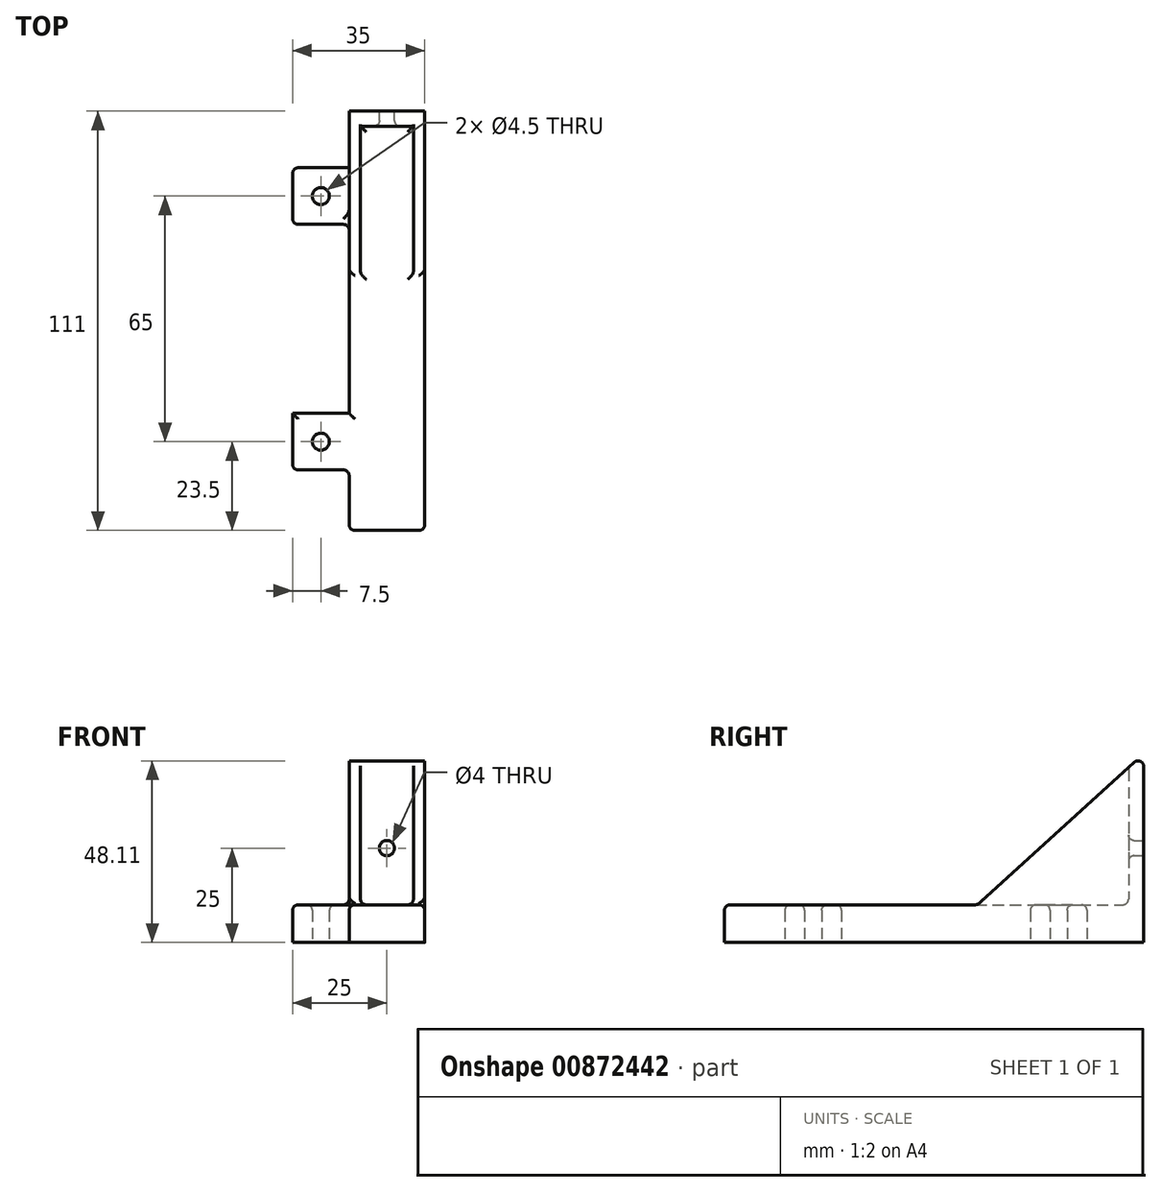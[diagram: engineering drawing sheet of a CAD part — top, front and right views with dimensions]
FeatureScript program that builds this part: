
annotation { "Feature Type Name" : "Feature", "Feature Type Description" : "" }
export const myFeature = defineFeature(function(context is Context, id is Id, definition is map)
    precondition{}
    {
        {
            var Q0;
            Q0=qCreatedBy(makeId("Top.planeOp"),FACE);
            var sketch = newSketch(context, id + "F0", { "sketchPlane" : qUnion([Q0])});
            skLineSegment(sketch, "E0", {"start": v(0, 0) * mm, "end": v(0, 55.5) * mm});
            skLineSegment(sketch, "E1", {"start": v(0, 55.5) * mm, "end": v(0, 33) * mm});
            skLineSegment(sketch, "E2", {"start": v(0, 33) * mm, "end": v(-15, 33) * mm});
            skLineSegment(sketch, "E3", {"start": v(-15, 33) * mm, "end": v(-15, 40.5) * mm});
            skLineSegment(sketch, "E4", {"start": v(-15, 40.5) * mm, "end": v(0, 40.5) * mm});
            skLineSegment(sketch, "E5", {"start": v(-15, 33) * mm, "end": v(-15, 25.5) * mm});
            skLineSegment(sketch, "E6", {"start": v(-15, 25.5) * mm, "end": v(0, 25.5) * mm});
            skLineSegment(sketch, "E7", {"start": v(0, 25.5) * mm, "end": v(-15, 40.5) * mm});
            skCircle(sketch, "E8", {"center": v(-7.5, 33) * mm, "radius": 2.25 * mm});
            skLineSegment(sketch, "E9", {"start": v(0, 55.5) * mm, "end": v(20, 55.5) * mm});
            skLineSegment(sketch, "E10", {"start": v(0, 0) * mm, "end": v(20, 0) * mm});
            skLineSegment(sketch, "E11", {"start": v(20, 0) * mm, "end": v(20, 55.5) * mm});
            skLineSegment(sketch, "E12", {"start": v(0, 0) * mm, "end": v(0, -22.5) * mm});
            skLineSegment(sketch, "E13", {"start": v(20, 0) * mm, "end": v(20, -55.5) * mm});
            skLineSegment(sketch, "E14", {"start": v(20, -55.5) * mm, "end": v(0, -55.5) * mm});
            skLineSegment(sketch, "E15", {"start": v(0, -55.5) * mm, "end": v(0, -22.5) * mm});
            skLineSegment(sketch, "E16", {"start": v(-15, -32) * mm, "end": v(-15, -24.5) * mm});
            skLineSegment(sketch, "E17", {"start": v(-15, -24.5) * mm, "end": v(0, -24.5) * mm});
            skLineSegment(sketch, "E18", {"start": v(-15, -32) * mm, "end": v(-15, -39.5) * mm});
            skLineSegment(sketch, "E19", {"start": v(-15, -39.5) * mm, "end": v(0, -39.5) * mm});
            skLineSegment(sketch, "E20", {"start": v(-15, -24.5) * mm, "end": v(0, -39.5) * mm});
            skLineSegment(sketch, "E21", {"start": v(-15, -32) * mm, "end": v(0, -32) * mm});
            skCircle(sketch, "E22", {"center": v(-7.5, -32) * mm, "radius": 2.25 * mm});
            skSolve(sketch);
        }
        {
            var Q0;
            {var subQ0=sQuery(id+"F0.wireOp",EDGE,"E2");var subQ1=sQuery(id+"F0.wireOp",EDGE,"E0");var subQ2=makeQuery(id+"F0.imprint","INTERSECT",VERTEX,{"derivedFrom":[subQ1,subQ0]});var subQ11=makeQuery(id+"F0.imprint","IMPRINT",EDGE,{"disambiguationData":[TD([[subQ2,-1.0]])],"derivedFrom":subQ0});var subQ12=sQuery(id+"F0.wireOp",EDGE,"E5");var subQ14=sQuery(id+"F0.wireOp",EDGE,"E3");var subQ16=sQuery(id+"F0.wireOp",EDGE,"E16");var subQ18=sQuery(id+"F0.wireOp",EDGE,"E17");var subQ19=sQuery(id+"F0.wireOp",EDGE,"E22");var subQ22=sQuery(id+"F0.wireOp",EDGE,"E21");var subQ23=sQuery(id+"F0.wireOp",EDGE,"E18");var subQ26=sQuery(id+"F0.wireOp",EDGE,"E4");var subQ31=sQuery(id+"F0.wireOp",EDGE,"E10");var subQ32=makeQuery(id+"F0.imprint","IMPRINT",EDGE,{"derivedFrom":subQ31});var subQ40=makeQuery(id+"F0.imprint","INTERSECT",VERTEX,{"disambiguationData":[OD(0.0)],"derivedFrom":[subQ22,subQ19]});var subQ41=makeQuery(id+"F0.imprint","IMPRINT",EDGE,{"disambiguationData":[TD([[subQ40,-1.0]])],"derivedFrom":subQ22});var subQ44=sQuery(id+"F0.wireOp",EDGE,"E9");Q0=qUnion([makeQuery(id+"F0.imprint","IMPRINT",FACE,{"disambiguationData":[TD([[makeQuery(id+"F0.imprint","IMPRINT",EDGE,{"derivedFrom":subQ23}),1.0]])]}),makeQuery(id+"F0.imprint","IMPRINT",FACE,{"disambiguationData":[TD([[subQ41,-1.0]])]}),makeQuery(id+"F0.imprint","IMPRINT",FACE,{"disambiguationData":[TD([[makeQuery(id+"F0.imprint","IMPRINT",EDGE,{"derivedFrom":subQ44}),-1.0]])]}),makeQuery(id+"F0.imprint","IMPRINT",FACE,{"disambiguationData":[TD([[makeQuery(id+"F0.imprint","IMPRINT",EDGE,{"derivedFrom":subQ26}),-1.0]])]}),makeQuery(id+"F0.imprint","IMPRINT",FACE,{"disambiguationData":[TD([[makeQuery(id+"F0.imprint","IMPRINT",EDGE,{"derivedFrom":subQ18}),-1.0]])]}),makeQuery(id+"F0.imprint","IMPRINT",FACE,{"disambiguationData":[TD([[subQ32,-1.0]])]}),makeQuery(id+"F0.imprint","IMPRINT",FACE,{"disambiguationData":[TD([[makeQuery(id+"F0.imprint","IMPRINT",EDGE,{"derivedFrom":subQ14}),-1.0]])]}),makeQuery(id+"F0.imprint","IMPRINT",FACE,{"disambiguationData":[TD([[makeQuery(id+"F0.imprint","IMPRINT",EDGE,{"derivedFrom":subQ16}),-1.0]])]}),makeQuery(id+"F0.imprint","IMPRINT",FACE,{"disambiguationData":[TD([[makeQuery(id+"F0.imprint","IMPRINT",EDGE,{"derivedFrom":subQ12}),1.0]])]}),makeQuery(id+"F0.imprint","IMPRINT",FACE,{"disambiguationData":[TD([[subQ11,1.0]])]})]);}
            extrude(context, id + "F1", {"entities" : qUnion([Q0]), "depth" : 10 * mm, "offsetDistance" : 25 * mm});
        }
        {
            var Q0;
            Q0=makeQuery(id+"F1.opExtrude","CAP_FACE",FACE,{"disambiguationData":[OSD([sQuery(id+"F0.wireOp",EDGE,"E0"),sQuery(id+"F0.wireOp",EDGE,"E3"),sQuery(id+"F0.wireOp",EDGE,"E4"),sQuery(id+"F0.wireOp",EDGE,"E5"),sQuery(id+"F0.wireOp",EDGE,"E6"),sQuery(id+"F0.wireOp",EDGE,"E8"),sQuery(id+"F0.wireOp",EDGE,"E9"),sQuery(id+"F0.wireOp",EDGE,"E11"),sQuery(id+"F0.wireOp",EDGE,"E12"),sQuery(id+"F0.wireOp",EDGE,"E13"),sQuery(id+"F0.wireOp",EDGE,"E14"),sQuery(id+"F0.wireOp",EDGE,"E15"),sQuery(id+"F0.wireOp",EDGE,"E16"),sQuery(id+"F0.wireOp",EDGE,"E17"),sQuery(id+"F0.wireOp",EDGE,"E18"),sQuery(id+"F0.wireOp",EDGE,"E19"),sQuery(id+"F0.wireOp",EDGE,"E22")])],"isStart":false});
            var sketch = newSketch(context, id + "F2", { "sketchPlane" : qUnion([Q0])});
            skLineSegment(sketch, "E23", {"start": v(0, 55.5) * mm, "end": v(0, 16.03) * mm});
            skLineSegment(sketch, "E24", {"start": v(0, 16.03) * mm, "end": v(20, 16.03) * mm});
            skLineSegment(sketch, "E25", {"start": v(20, 16.03) * mm, "end": v(20, 55.5) * mm});
            skLineSegment(sketch, "E26", {"start": v(20, 55.5) * mm, "end": v(0, 55.5) * mm});
            skLineSegment(sketch, "E27", {"start": v(0, 16.03) * mm, "end": v(3, 16.03) * mm});
            skLineSegment(sketch, "E28", {"start": v(20, 16.03) * mm, "end": v(17, 16.03) * mm});
            skLineSegment(sketch, "E29", {"start": v(0, 55.5) * mm, "end": v(0, 51.5) * mm});
            skLineSegment(sketch, "E30", {"start": v(0, 51.5) * mm, "end": v(0, 55.5) * mm});
            skLineSegment(sketch, "E31", {"start": v(0, 51.5) * mm, "end": v(20, 51.5) * mm});
            skLineSegment(sketch, "E32", {"start": v(17, 16.03) * mm, "end": v(17, 51.5) * mm});
            skLineSegment(sketch, "E33", {"start": v(3, 16.03) * mm, "end": v(3, 51.5) * mm});
            skLineSegment(sketch, "E34", {"start": v(20, 51.5) * mm, "end": v(20, 55.5) * mm});
            skSolve(sketch);
        }
        {
            var Q0;
            Q0=makeQuery(id+"F2.imprint","IMPRINT",FACE,{"disambiguationData":[TD([[makeQuery(id+"F2.imprint","IMPRINT",EDGE,{"derivedFrom":sQuery(id+"F2.wireOp",EDGE,"E26")}),-1.0]])]});
            extrude(context, id + "F3", {"entities" : qUnion([Q0]), "operationType" : NewBodyOperationType.ADD, "depth" : 40 * mm, "offsetDistance" : 25 * mm});
        }
        {
            var Q0;
            Q0=makeQuery(id+"F3.opExtrude","SWEPT_FACE",FACE,{"disambiguationData":[OSD([sQuery(id+"F2.wireOp",EDGE,"E31")])]});
            var sketch = newSketch(context, id + "F4", { "sketchPlane" : qUnion([Q0])});
            skLineSegment(sketch, "E35", {"start": v(0, 50) * mm, "end": v(0, 10) * mm});
            skLineSegment(sketch, "E36", {"start": v(0, 50) * mm, "end": v(3, 50) * mm});
            skLineSegment(sketch, "E37", {"start": v(3, 50) * mm, "end": v(3, 10) * mm});
            skLineSegment(sketch, "E38", {"start": v(20, 50) * mm, "end": v(17, 50) * mm});
            skLineSegment(sketch, "E39", {"start": v(17, 50) * mm, "end": v(17, 10) * mm});
            skPoint(sketch, "E39.endSnap0", {"position": v(10, 10) * mm});
            skSolve(sketch);
        }
        {
            var Q0;
            Q0 = qSketchRegion(id + "F4", true);
            var Q1;
            {var subQ0=sQuery(id+"F4.wireOp",EDGE,"E35");Q1=makeQuery(id+"F4.imprint","IMPRINT",FACE,{"disambiguationData":[TD([[makeQuery(id+"F4.imprint","IMPRINT",EDGE,{"derivedFrom":subQ0}),1.0]])]});}
            var Q2;
            Q2=makeQuery(id+"F4.imprint","IMPRINT",FACE,{"disambiguationData":[TD([[makeQuery(id+"F4.imprint","IMPRINT",EDGE,{"derivedFrom":sQuery(id+"F4.wireOp",EDGE,"E38")}),-1.0]])]});
            extrude(context, id + "F5", {"entities" : qUnion([Q0, Q1, Q2]), "operationType" : NewBodyOperationType.ADD, "depth" : 40 * mm, "offsetDistance" : 25 * mm});
        }
        {
            var Q0;
            {var subQ0=sQuery(id+"F0.wireOp",EDGE,"E0");Q0=makeQuery(id+"F5.boolean.opBoolean","MERGE",FACE,{"derivedFrom":[makeQuery(id+"F1.opExtrude","SWEPT_FACE",FACE,{"disambiguationData":[OSD([subQ0,sQuery(id+"F0.wireOp",EDGE,"E12"),sQuery(id+"F0.wireOp",EDGE,"E15")])]}),makeQuery(id+"F3.boolean.opBoolean","MERGE",FACE,{"derivedFrom":[makeQuery(id+"F1.opExtrude","SWEPT_FACE",FACE,{"disambiguationData":[OSD([subQ0])]}),makeQuery(id+"F3.opExtrude","SWEPT_FACE",FACE,{"disambiguationData":[OSD([sQuery(id+"F2.wireOp",EDGE,"E30")])]})]}),makeQuery(id+"F5.opExtrude","SWEPT_FACE",FACE,{"disambiguationData":[OSD([sQuery(id+"F4.wireOp",EDGE,"E35")])]})]});}
            var sketch = newSketch(context, id + "F6", { "sketchPlane" : qUnion([Q0])});
            skLineSegment(sketch, "E40", {"start": v(-11.5, 10) * mm, "end": v(-55.5, 50) * mm});
            skSolve(sketch);
        }
        {
            var Q0;
            Q0=makeQuery(id+"F6.imprint","IMPRINT",FACE,{"disambiguationData":[TD([[makeQuery(id+"F6.imprint","IMPRINT",EDGE,{"derivedFrom":sQuery(id+"F6.wireOp",EDGE,"E40")}),-1.0]])]});
            extrude(context, id + "F7", {"entities" : qUnion([Q0]), "operationType" : NewBodyOperationType.REMOVE, "oppositeDirection" : true, "depth" : 25 * mm, "offsetDistance" : 25 * mm});
        }
        {
            var Q0;
            Q0=makeQuery(id+"F3.boolean.opBoolean","MERGE",FACE,{"derivedFrom":[makeQuery(id+"F1.opExtrude","SWEPT_FACE",FACE,{"disambiguationData":[OSD([sQuery(id+"F0.wireOp",EDGE,"E9")])]}),makeQuery(id+"F3.opExtrude","SWEPT_FACE",FACE,{"disambiguationData":[OSD([sQuery(id+"F2.wireOp",EDGE,"E26")])]})]});
            var sketch = newSketch(context, id + "F8", { "sketchPlane" : qUnion([Q0])});
            skLineSegment(sketch, "E41", {"start": v(0, 50) * mm, "end": v(-20, 50) * mm});
            skLineSegment(sketch, "E42", {"start": v(-10, 25) * mm, "end": v(-10, 50) * mm});
            skLineSegment(sketch, "E43", {"start": v(-10, 50) * mm, "end": v(-10, 0) * mm});
            skLineSegment(sketch, "E44", {"start": v(-10, 50) * mm, "end": v(-10, 40) * mm});
            skCircle(sketch, "E45", {"center": v(-10, 25) * mm, "radius": 2 * mm});
            skCircle(sketch, "E46", {"center": v(-10, 40) * mm, "radius": 2 * mm});
            skSolve(sketch);
        }
        {
            var Q0;
            {var subQ0=sQuery(id+"F8.wireOp",EDGE,"E43");var subQ1=makeQuery(id+"F8.imprint","IMPRINT",VERTEX,{"derivedFrom":subQ0});Q0=makeQuery(id+"F8.imprint","IMPRINT",FACE,{"disambiguationData":[TD([[makeQuery(id+"F8.imprint","IMPRINT",EDGE,{"disambiguationData":[TD([[subQ1,1.0]])],"derivedFrom":subQ0}),-1.0]])]});}
            var Q1;
            {var subQ0=sQuery(id+"F8.wireOp",EDGE,"E43");var subQ1=makeQuery(id+"F8.imprint","IMPRINT",VERTEX,{"derivedFrom":subQ0});Q1=makeQuery(id+"F8.imprint","IMPRINT",FACE,{"disambiguationData":[TD([[makeQuery(id+"F8.imprint","IMPRINT",EDGE,{"disambiguationData":[TD([[subQ1,1.0]])],"derivedFrom":subQ0}),1.0]])]});}
            var Q2;
            {var subQ0=sQuery(id+"F8.wireOp",EDGE,"E44");var subQ1=sQuery(id+"F8.wireOp",EDGE,"E43");var subQ2=makeQuery(id+"F8.imprint","INTERSECT",VERTEX,{"derivedFrom":[subQ1,subQ0]});Q2=makeQuery(id+"F8.imprint","IMPRINT",FACE,{"disambiguationData":[TD([[makeQuery(id+"F8.imprint","IMPRINT",EDGE,{"disambiguationData":[TD([[subQ2,-1.0]])],"derivedFrom":subQ1}),1.0]])]});}
            var Q3;
            {var subQ0=sQuery(id+"F8.wireOp",EDGE,"E44");var subQ1=sQuery(id+"F8.wireOp",EDGE,"E43");var subQ2=makeQuery(id+"F8.imprint","INTERSECT",VERTEX,{"derivedFrom":[subQ1,subQ0]});Q3=makeQuery(id+"F8.imprint","IMPRINT",FACE,{"disambiguationData":[TD([[makeQuery(id+"F8.imprint","IMPRINT",EDGE,{"disambiguationData":[TD([[subQ2,-1.0]])],"derivedFrom":subQ1}),-1.0]])]});}
            var Q4;
            Q4=sQuery(id+"F8.wireOp",EDGE,"E45");
            var Q5;
            Q5=sQuery(id+"F8.wireOp",EDGE,"E46");
            extrude(context, id + "F9", {"entities" : qUnion([Q0, Q1, Q2, Q3]), "operationType" : NewBodyOperationType.REMOVE, "surfaceEntities" : qUnion([Q4, Q5]), "oppositeDirection" : true, "depth" : 25 * mm, "offsetDistance" : 25 * mm});
        }
        {
            var Q0;
            Q0=makeQuery(id+"F1.opExtrude","CAP_EDGE",EDGE,{"disambiguationData":[OSD([sQuery(id+"F0.wireOp",EDGE,"E11"),sQuery(id+"F0.wireOp",EDGE,"E13")])],"isStart":false});
            var Q1;
            Q1=makeQuery(id+"F1.opExtrude","CAP_EDGE",EDGE,{"disambiguationData":[OSD([sQuery(id+"F0.wireOp",EDGE,"E0"),sQuery(id+"F0.wireOp",EDGE,"E12"),sQuery(id+"F0.wireOp",EDGE,"E15")])],"isStart":false});
            var Q2;
            Q2=makeQuery(id+"F1.opExtrude","CAP_EDGE",EDGE,{"disambiguationData":[OSD([sQuery(id+"F0.wireOp",EDGE,"E17")])],"isStart":false});
            var Q3;
            Q3=makeQuery(id+"F1.opExtrude","CAP_EDGE",EDGE,{"disambiguationData":[OSD([sQuery(id+"F0.wireOp",EDGE,"E15")])],"isStart":false});
            var Q4;
            Q4=makeQuery(id+"F1.opExtrude","CAP_EDGE",EDGE,{"disambiguationData":[OSD([sQuery(id+"F0.wireOp",EDGE,"E16"),sQuery(id+"F0.wireOp",EDGE,"E18")])],"isStart":false});
            var Q5;
            Q5=makeQuery(id+"F1.opExtrude","CAP_EDGE",EDGE,{"disambiguationData":[OSD([sQuery(id+"F0.wireOp",EDGE,"E14")])],"isStart":false});
            var Q6;
            Q6=makeQuery(id+"F1.opExtrude","CAP_EDGE",EDGE,{"disambiguationData":[OSD([sQuery(id+"F0.wireOp",EDGE,"E6")])],"isStart":false});
            var Q7;
            Q7=makeQuery(id+"F1.opExtrude","CAP_EDGE",EDGE,{"disambiguationData":[OSD([sQuery(id+"F0.wireOp",EDGE,"E3"),sQuery(id+"F0.wireOp",EDGE,"E5")])],"isStart":false});
            var Q8;
            Q8=makeQuery(id+"F1.opExtrude","CAP_EDGE",EDGE,{"disambiguationData":[OSD([sQuery(id+"F0.wireOp",EDGE,"E4")])],"isStart":false});
            var Q9;
            {var subQ0=sQuery(id+"F0.wireOp",EDGE,"E22");var subQ1=sQuery(id+"F0.wireOp",EDGE,"E18");var subQ2=sQuery(id+"F0.wireOp",EDGE,"E16");var subQ3=sQuery(id+"F0.wireOp",EDGE,"E15");var subQ4=sQuery(id+"F0.wireOp",EDGE,"E17");var subQ5=sQuery(id+"F0.wireOp",EDGE,"E12");var subQ6=sQuery(id+"F0.wireOp",EDGE,"E0");var subQ8=sQuery(id+"F0.wireOp",EDGE,"E19");var subQ12=sQuery(id+"F0.wireOp",EDGE,"E13");var subQ13=sQuery(id+"F0.wireOp",EDGE,"E11");var subQ14=sQuery(id+"F0.wireOp",EDGE,"E14");Q9=makeQuery(id+"F5.boolean.opBoolean","SPLIT",FACE,{"disambiguationData":[TD([makeQuery(id+"F1.opExtrude","SWEPT_FACE",FACE,{"disambiguationData":[OSD([subQ14])]})])],"derivedFrom":makeQuery(id+"F1.opExtrude","CAP_FACE",FACE,{"disambiguationData":[OSD([subQ6,sQuery(id+"F0.wireOp",EDGE,"E3"),sQuery(id+"F0.wireOp",EDGE,"E4"),sQuery(id+"F0.wireOp",EDGE,"E5"),sQuery(id+"F0.wireOp",EDGE,"E6"),sQuery(id+"F0.wireOp",EDGE,"E8"),sQuery(id+"F0.wireOp",EDGE,"E9"),subQ13,subQ5,subQ12,subQ14,subQ3,subQ2,subQ4,subQ1,subQ8,subQ0])],"isStart":false})});}
            var Q10;
            Q10=makeQuery(id+"F7.boolean.opBoolean","INTERSECT",EDGE,{"derivedFrom":[makeQuery(id+"F3.opExtrude","SWEPT_FACE",FACE,{"disambiguationData":[OSD([sQuery(id+"F2.wireOp",EDGE,"E31")])]}),makeQuery(id+"F7.opExtrude","SWEPT_FACE",FACE,{"disambiguationData":[OSD([sQuery(id+"F6.wireOp",EDGE,"E40")])]})]});
            var Q11;
            {var subQ0=sQuery(id+"F2.wireOp",EDGE,"E26");Q11=makeQuery(id+"F7.boolean.opBoolean","MERGE",EDGE,{"derivedFrom":[makeQuery(id+"F3.opExtrude","CAP_EDGE",EDGE,{"disambiguationData":[OSD([subQ0])],"isStart":false})],"fromTools":[makeQuery(id+"F7.opExtrude","SWEPT_EDGE",EDGE,{"disambiguationData":[OSD([sQuery(id+"F0.wireOp",EDGE,"E0"),sQuery(id+"F0.wireOp",EDGE,"E9"),subQ0,sQuery(id+"F2.wireOp",EDGE,"E30"),sQuery(id+"F4.wireOp",EDGE,"E35"),sQuery(id+"F4.wireOp",EDGE,"E36"),sQuery(id+"F6.wireOp",EDGE,"E40")])]})]});}
            var Q12;
            Q12=makeQuery(id+"F1.opExtrude","SWEPT_EDGE",EDGE,{"disambiguationData":[OSD([sQuery(id+"F0.wireOp",EDGE,"E18"),sQuery(id+"F0.wireOp",EDGE,"E19")])]});
            var Q13;
            Q13=makeQuery(id+"F1.opExtrude","SWEPT_EDGE",EDGE,{"disambiguationData":[OSD([sQuery(id+"F0.wireOp",EDGE,"E15"),sQuery(id+"F0.wireOp",EDGE,"E19"),sQuery(id+"F0.wireOp",EDGE,"E20")])]});
            var Q14;
            Q14=makeQuery(id+"F1.opExtrude","SWEPT_EDGE",EDGE,{"disambiguationData":[OSD([sQuery(id+"F0.wireOp",EDGE,"E14"),sQuery(id+"F0.wireOp",EDGE,"E15")])]});
            var Q15;
            Q15=makeQuery(id+"F1.opExtrude","SWEPT_EDGE",EDGE,{"disambiguationData":[OSD([sQuery(id+"F0.wireOp",EDGE,"E13"),sQuery(id+"F0.wireOp",EDGE,"E14")])]});
            var Q16;
            Q16=makeQuery(id+"F1.opExtrude","SWEPT_EDGE",EDGE,{"disambiguationData":[OSD([sQuery(id+"F0.wireOp",EDGE,"E0"),sQuery(id+"F0.wireOp",EDGE,"E6"),sQuery(id+"F0.wireOp",EDGE,"E7")])]});
            var Q17;
            Q17=makeQuery(id+"F1.opExtrude","SWEPT_EDGE",EDGE,{"disambiguationData":[OSD([sQuery(id+"F0.wireOp",EDGE,"E5"),sQuery(id+"F0.wireOp",EDGE,"E6")])]});
            var Q18;
            Q18=makeQuery(id+"F1.opExtrude","SWEPT_EDGE",EDGE,{"disambiguationData":[OSD([sQuery(id+"F0.wireOp",EDGE,"E3"),sQuery(id+"F0.wireOp",EDGE,"E4"),sQuery(id+"F0.wireOp",EDGE,"E7")])]});
            var Q19;
            Q19=makeQuery(id+"F1.opExtrude","CAP_EDGE",EDGE,{"disambiguationData":[OSD([sQuery(id+"F0.wireOp",EDGE,"E8")])],"isStart":false});
            var Q20;
            Q20=makeQuery(id+"F9.boolean.opBoolean","INTERSECT",EDGE,{"derivedFrom":[makeQuery(id+"F3.opExtrude","SWEPT_FACE",FACE,{"disambiguationData":[OSD([sQuery(id+"F2.wireOp",EDGE,"E31")])]}),makeQuery(id+"F9.opExtrude","SWEPT_FACE",FACE,{"disambiguationData":[OSD([sQuery(id+"F8.wireOp",EDGE,"E46")])]})]});
            var Q21;
            Q21=makeQuery(id+"F9.boolean.opBoolean","INTERSECT",EDGE,{"derivedFrom":[makeQuery(id+"F3.opExtrude","SWEPT_FACE",FACE,{"disambiguationData":[OSD([sQuery(id+"F2.wireOp",EDGE,"E31")])]}),makeQuery(id+"F9.opExtrude","SWEPT_FACE",FACE,{"disambiguationData":[OSD([sQuery(id+"F8.wireOp",EDGE,"E45")])]})]});
            fillet(context, id + "F10", {"entities" : qUnion([Q0, Q1, Q2, Q3, Q4, Q5, Q6, Q7, Q8, Q9, Q10, Q11, Q12, Q13, Q14, Q15, Q16, Q17, Q18, Q19, Q20, Q21]), "radius" : 1.5 * mm, "tangentPropagation" : true, "allowEdgeOverflow" : false});
        }
    });
